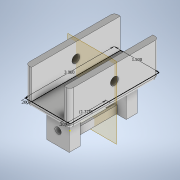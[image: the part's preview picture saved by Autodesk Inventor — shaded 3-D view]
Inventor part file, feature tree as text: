
AUTODESK INVENTOR PART (.ipt)
format: ipt  version: 2020 (Build 240168000, 168)  size: 670,208 bytes
history: native  units: in
note: dims shown in document units (in); Inventor stores cm internally (conversion verified against a paired STEP export)
features: sketch x8, extrude x5, hole x4, fillet x1, plane x1, mirror x1
ambient origin geometry x8: Origin, YZ Plane, XZ Plane, XY Plane, X Axis, Y Axis, Z Axis, Center Point
bodies: Solid1 (feature_tree)
feature tree (20):
  sketch  "Sketch1"  dims[d0=1.5in d1=3.0in]
  extrude  "Extrusion1"  Depth=3.0in
  extrude  "Extrusion2"  Depth=0.2in
  hole  "Hole1"  [1 undecoded]
  extrude  "Extrusion3"  Depth=1.0in
  hole  "Hole2"  [1 undecoded]
  fillet  "Fillet1"  Radius=0.125in
  extrude  "Extrusion4"  Depth=1.0in TaperAngle=0.0deg
  extrude  "Extrusion5"  Depth=0.125in
  hole  "Hole3"  [1 undecoded]
  hole  "Hole4"  [1 undecoded]
  sketch  "Sketch9"  dims[d23=0.45in d24=0.0787in d25=0.75in d26=0.438in d27=0.25in d28=0.5635in d29=1.0in d30=0.8108in d31=0.125in d32=0.125in d33=0.125in d34=0.5in d35=0.5in d36=90.0deg d37=0.1in d38=0.1in d39=0.125in d40=0.075in d41=0.25in d42=1.6in d43=0.0in d44=0.05in d45=0.0in d46=0.5in d47=0.5in d48=0.5in d49=0.375in d50=0.375in d51=0.375in d52=0.213in d53=0.75in d54=0.119in d55=0.25in d56=0.5635in d57=0.25in d58=0.0in d59=0.176in d60=0.75in d61=0.119in d62=0.25in d63=0.5635in d64=0.08in d65=0.0in d66=1.375in]
  plane  "Work Plane1"
  mirror  "Mirror1"
  sketch  "Sketch2"  dims[d2=0.2in d3=0.2in]
  sketch  "Sketch3"  dims[d4=1.0in d5=0.0in d6=0.2in d7=0.0in]
  sketch  "Sketch5"  dims[d8=0.5in]
  sketch  "Sketch6"  dims[d9=0.266in d10=0.75in d11=0.438in d12=0.25in d13=0.5635in d14=1.0in d15=0.8108in d16=0.5in]
  sketch  "Sketch7"  dims[d17=1.0in d18=0.75in d19=0.125in]
  sketch  "Sketch8"  dims[d20=0.125in d21=1.0in d22=0.0in]
note: 4 required parameter values undecoded (feature->parameter linkage not recoverable at this tier; creation-order binding heuristic only, values carry confidence <= 0.55)
